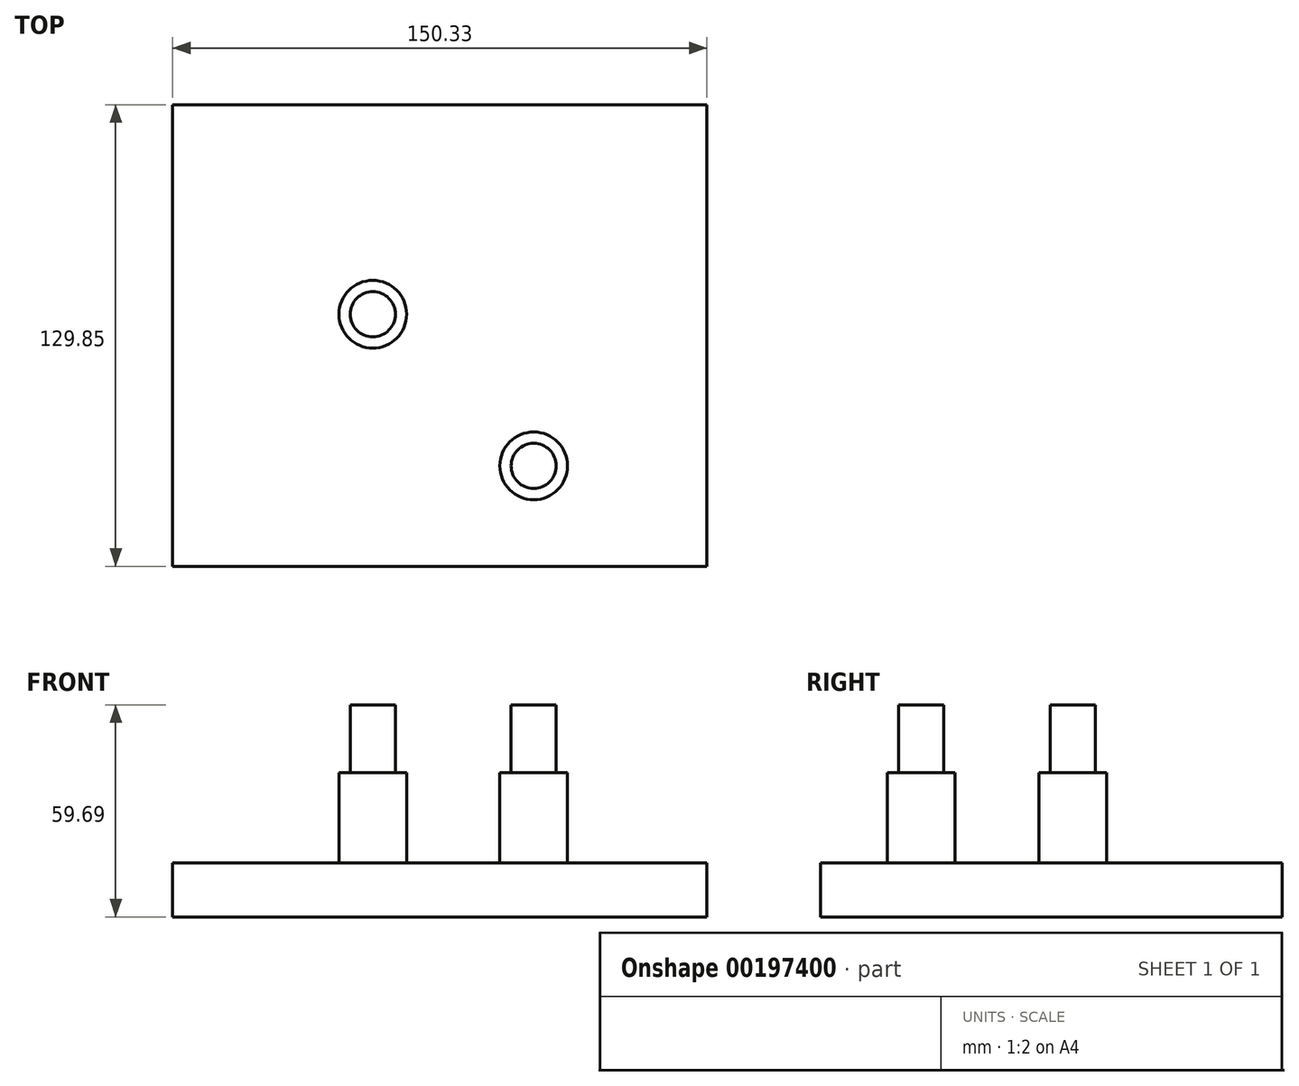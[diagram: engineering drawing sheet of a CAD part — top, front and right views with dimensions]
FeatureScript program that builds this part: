
annotation { "Feature Type Name" : "Feature", "Feature Type Description" : "" }
export const myFeature = defineFeature(function(context is Context, id is Id, definition is map)
    precondition{}
    {
        {
            var Q0;
            Q0=qCreatedBy(makeId("Top.planeOp"),FACE);
            var sketch = newSketch(context, id + "F0", { "sketchPlane" : qUnion([Q0])});
            skLineSegment(sketch, "E0.bottom", {"start": v(101.6, 101.6) * mm, "end": v(-101.6, 101.6) * mm});
            skLineSegment(sketch, "E0.top", {"start": v(101.6, -101.6) * mm, "end": v(-101.6, -101.6) * mm});
            skLineSegment(sketch, "E0.left", {"start": v(101.6, 101.6) * mm, "end": v(101.6, -101.6) * mm});
            skLineSegment(sketch, "E0.right", {"start": v(-101.6, 101.6) * mm, "end": v(-101.6, -101.6) * mm});
            skPoint(sketch, "E0.middle", {"position": v(0, 0) * mm});
            skSolve(sketch);
        }
        {
            var Q0;
            Q0 = qSketchRegion(id + "F0", true);
            extrude(context, id + "F1", {"entities" : qUnion([Q0]), "depth" : 15.24 * mm});
        }
        {
            var Q0;
            Q0=makeQuery(id+"F1.opExtrude","CAP_FACE",FACE,{"disambiguationData":[OSD([sQuery(id+"F0.wireOp",EDGE,"E0.bottom"),sQuery(id+"F0.wireOp",EDGE,"E0.top"),sQuery(id+"F0.wireOp",EDGE,"E0.left"),sQuery(id+"F0.wireOp",EDGE,"E0.right")])],"isStart":false});
            var sketch = newSketch(context, id + "F2", { "sketchPlane" : qUnion([Q0])});
            skCircle(sketch, "E1", {"center": v(0, 0) * mm, "radius": 9.53 * mm});
            skCircle(sketch, "E2", {"center": v(62.23, 0) * mm, "radius": 9.53 * mm});
            skLineSegment(sketch, "E3", {"start": v(0, 0) * mm, "end": v(62.23, 0) * mm, "construction": true});
            skLineSegment(sketch, "E4", {"start": v(62.23, 0) * mm, "end": v(62.23, -62.23) * mm, "construction": true});
            skLineSegment(sketch, "E5", {"start": v(0, 0) * mm, "end": v(-45.3, 42.67) * mm, "construction": true});
            skCircle(sketch, "E6", {"center": v(-45.3, 42.67) * mm, "radius": 9.53 * mm});
            skCircle(sketch, "E7", {"center": v(62.23, -62.23) * mm, "radius": 9.53 * mm});
            skSolve(sketch);
        }
        {
            var Q0;
            Q0 = qSketchRegion(id + "F2", true);
            extrude(context, id + "F3", {"entities" : qUnion([Q0]), "operationType" : NewBodyOperationType.ADD, "depth" : 25.4 * mm});
        }
        {
            var Q0;
            Q0=makeQuery(id+"F3.opExtrude","CAP_FACE",FACE,{"disambiguationData":[OSD([sQuery(id+"F2.wireOp",EDGE,"E6")])],"isStart":false});
            var sketch = newSketch(context, id + "F4", { "sketchPlane" : qUnion([Q0])});
            skCircle(sketch, "E8", {"center": v(-45.3, 42.67) * mm, "radius": 6.35 * mm});
            skCircle(sketch, "E9", {"center": v(0, 0) * mm, "radius": 6.35 * mm});
            skCircle(sketch, "E10", {"center": v(62.23, -62.23) * mm, "radius": 6.35 * mm});
            skCircle(sketch, "E11", {"center": v(62.23, 0) * mm, "radius": 6.35 * mm});
            skSolve(sketch);
        }
        {
            var Q0;
            Q0 = qSketchRegion(id + "F4", true);
            extrude(context, id + "F5", {"entities" : qUnion([Q0]), "operationType" : NewBodyOperationType.ADD, "depth" : 19.05 * mm});
        }
        {
            var Q0;
            Q0=makeQuery(id+"F1.opExtrude","CAP_FACE",FACE,{"disambiguationData":[OSD([sQuery(id+"F0.wireOp",EDGE,"E0.bottom"),sQuery(id+"F0.wireOp",EDGE,"E0.top"),sQuery(id+"F0.wireOp",EDGE,"E0.left"),sQuery(id+"F0.wireOp",EDGE,"E0.right")])],"isStart":false});
            var sketch = newSketch(context, id + "F6", { "sketchPlane" : qUnion([Q0])});
            skLineSegment(sketch, "E12", {"start": v(0, 0) * mm, "end": v(-42.09, -45.84) * mm, "construction": true});
            skCircle(sketch, "E13", {"center": v(-42.09, -45.84) * mm, "radius": 9.53 * mm});
            skSolve(sketch);
        }
        {
            var Q0;
            Q0 = qSketchRegion(id + "F6", true);
            extrude(context, id + "F7", {"entities" : qUnion([Q0]), "operationType" : NewBodyOperationType.ADD, "depth" : 25.4 * mm});
        }
        {
            var Q0;
            Q0=makeQuery(id+"F7.opExtrude","CAP_FACE",FACE,{"disambiguationData":[OSD([sQuery(id+"F6.wireOp",EDGE,"E13")])],"isStart":false});
            var sketch = newSketch(context, id + "F8", { "sketchPlane" : qUnion([Q0])});
            skCircle(sketch, "E14", {"center": v(-42.09, -45.84) * mm, "radius": 6.35 * mm});
            skSolve(sketch);
        }
        {
            var Q0;
            Q0 = qSketchRegion(id + "F8", true);
            extrude(context, id + "F9", {"entities" : qUnion([Q0]), "operationType" : NewBodyOperationType.ADD, "depth" : 19.05 * mm});
        }
        {
            var Q0;
            Q0=makeQuery(id+"F5.opExtrude","CAP_FACE",FACE,{"disambiguationData":[OSD([sQuery(id+"F4.wireOp",EDGE,"E11")])],"isStart":false});
            var sketch = newSketch(context, id + "F10", { "sketchPlane" : qUnion([Q0])});
            skLineSegment(sketch, "E15.bottom", {"start": v(114.74, 105.97) * mm, "end": v(48.73, 105.97) * mm});
            skLineSegment(sketch, "E15.top", {"start": v(114.74, -121.7) * mm, "end": v(48.73, -121.7) * mm});
            skLineSegment(sketch, "E15.left", {"start": v(114.74, 105.97) * mm, "end": v(114.74, -121.7) * mm});
            skLineSegment(sketch, "E15.right", {"start": v(48.73, 105.97) * mm, "end": v(48.73, -121.7) * mm});
            skSolve(sketch);
        }
        {
            var Q0;
            Q0 = qSketchRegion(id + "F10", true);
            extrude(context, id + "F11", {"entities" : qUnion([Q0]), "operationType" : NewBodyOperationType.REMOVE, "oppositeDirection" : true, "depth" : 81.8 * mm});
        }
        {
            var Q0;
            Q0=makeQuery(id+"F1.opExtrude","CAP_FACE",FACE,{"disambiguationData":[OSD([sQuery(id+"F0.wireOp",EDGE,"E0.bottom"),sQuery(id+"F0.wireOp",EDGE,"E0.top"),sQuery(id+"F0.wireOp",EDGE,"E0.left"),sQuery(id+"F0.wireOp",EDGE,"E0.right")])],"isStart":false});
            var sketch = newSketch(context, id + "F12", { "sketchPlane" : qUnion([Q0])});
            skLineSegment(sketch, "E16.bottom", {"start": v(-113.85, -28.25) * mm, "end": v(57.95, -28.25) * mm});
            skLineSegment(sketch, "E16.top", {"start": v(-113.85, -116.1) * mm, "end": v(57.95, -116.1) * mm});
            skLineSegment(sketch, "E16.left", {"start": v(-113.85, -28.25) * mm, "end": v(-113.85, -116.1) * mm});
            skLineSegment(sketch, "E16.right", {"start": v(57.95, -28.25) * mm, "end": v(57.95, -116.1) * mm});
            skLineSegment(sketch, "E17.bottom", {"start": v(-15.06, -28.25) * mm, "end": v(-15.03, -28.25) * mm});
            skLineSegment(sketch, "E17.top", {"start": v(-15.06, -34.22) * mm, "end": v(-15.03, -34.22) * mm});
            skLineSegment(sketch, "E17.left", {"start": v(-15.06, -28.25) * mm, "end": v(-15.06, -34.22) * mm});
            skLineSegment(sketch, "E17.right", {"start": v(-15.03, -28.25) * mm, "end": v(-15.03, -34.22) * mm});
            skSolve(sketch);
        }
        {
            var Q0;
            Q0 = qSketchRegion(id + "F12", true);
            extrude(context, id + "F13", {"entities" : qUnion([Q0]), "operationType" : NewBodyOperationType.REMOVE, "endBound" : BoundingType.SYMMETRIC, "oppositeDirection" : true, "depth" : 118.36 * mm});
        }
    });
